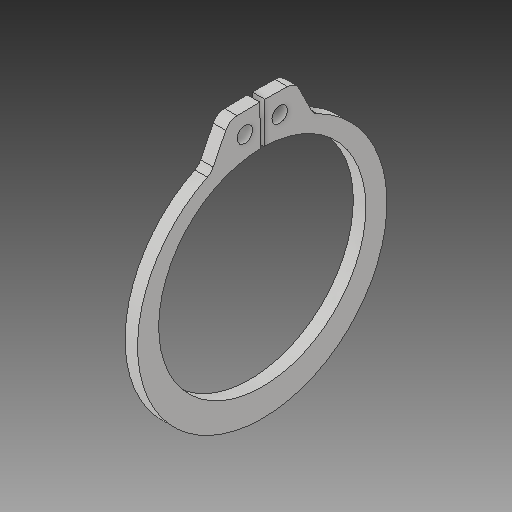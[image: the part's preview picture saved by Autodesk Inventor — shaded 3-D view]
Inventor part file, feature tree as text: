
AUTODESK INVENTOR PART (.ipt)
format: ipt  version: 2017 (Build 210142000, 142)  size: 110,080 bytes
history: native  units: in
note: dims shown in document units (in); Inventor stores cm internally (conversion verified against a paired STEP export)
features: fillet x1
ambient origin geometry x8: Origin, YZ Plane, XZ Plane, XY Plane, X Axis, Y Axis, Z Axis, Center Point
bodies: Solid1 (feature_tree)
feature tree (1):
  fillet  "Fillet1"  [1 undecoded]
note: 1 required parameter value undecoded (feature->parameter linkage not recoverable at this tier; creation-order binding heuristic only, values carry confidence <= 0.55)
